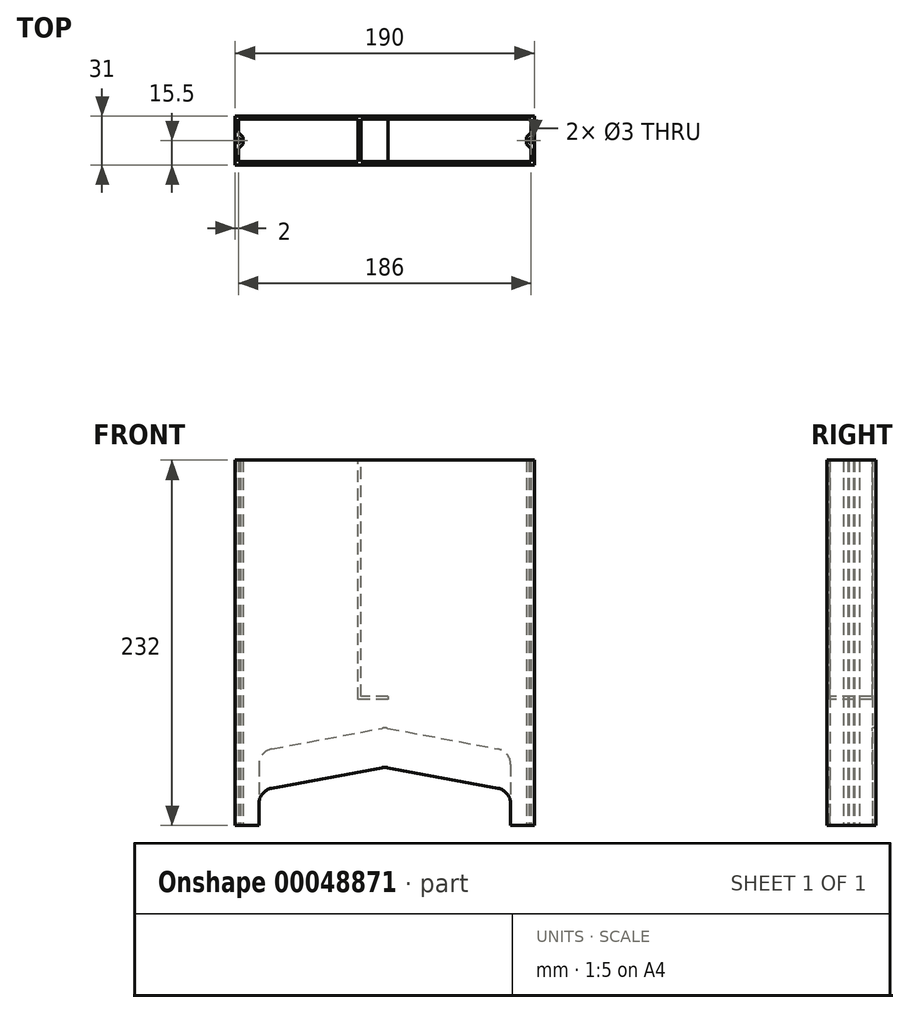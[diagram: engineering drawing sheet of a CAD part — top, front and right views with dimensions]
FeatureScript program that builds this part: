
annotation { "Feature Type Name" : "Feature", "Feature Type Description" : "" }
export const myFeature = defineFeature(function(context is Context, id is Id, definition is map)
    precondition{}
    {
        {
            var Q0;
            Q0=qCreatedBy(makeId("Top.planeOp"),FACE);
            var sketch = newSketch(context, id + "F0", { "sketchPlane" : qUnion([Q0])});
            skLineSegment(sketch, "E0.bottom", {"start": v(0, 0) * mm, "end": v(190, 0) * mm});
            skLineSegment(sketch, "E0.top", {"start": v(0, 31) * mm, "end": v(190, 31) * mm});
            skLineSegment(sketch, "E0.left", {"start": v(0, 0) * mm, "end": v(0, 31) * mm});
            skLineSegment(sketch, "E0.right", {"start": v(190, 0) * mm, "end": v(190, 31) * mm});
            skLineSegment(sketch, "E1.bottom", {"start": v(2, 2) * mm, "end": v(188, 2) * mm});
            skLineSegment(sketch, "E1.top", {"start": v(2, 29) * mm, "end": v(188, 29) * mm});
            skLineSegment(sketch, "E2", {"start": v(2, 29) * mm, "end": v(2, 20.62) * mm});
            skLineSegment(sketch, "E3", {"start": v(2, 20.62) * mm, "end": v(5, 17.62) * mm});
            skLineSegment(sketch, "E4", {"start": v(5, 17.62) * mm, "end": v(5, 13.38) * mm});
            skLineSegment(sketch, "E5", {"start": v(5, 13.38) * mm, "end": v(2, 10.38) * mm});
            skLineSegment(sketch, "E6", {"start": v(2, 10.38) * mm, "end": v(2, 2) * mm});
            skLineSegment(sketch, "E7", {"start": v(2, 20.62) * mm, "end": v(2, 10.38) * mm, "construction": true});
            skCircle(sketch, "E8", {"center": v(2, 15.5) * mm, "radius": 1.5 * mm});
            skLineSegment(sketch, "E9", {"start": v(95, 29) * mm, "end": v(95, 2) * mm, "construction": true});
            skLineSegment(sketch, "E10.MirrorCS", {"start": v(188, 10.38) * mm, "end": v(188, 2) * mm});
            skLineSegment(sketch, "E11.MirrorCS", {"start": v(185, 13.38) * mm, "end": v(188, 10.38) * mm});
            skLineSegment(sketch, "E12.MirrorCS", {"start": v(185, 17.62) * mm, "end": v(185, 13.38) * mm});
            skCircle(sketch, "E13.MirrorC", {"center": v(188, 15.5) * mm, "radius": 1.5 * mm});
            skLineSegment(sketch, "E14.MirrorCS", {"start": v(188, 29) * mm, "end": v(188, 20.62) * mm});
            skLineSegment(sketch, "E15.MirrorCS", {"start": v(188, 20.62) * mm, "end": v(185, 17.62) * mm});
            skSolve(sketch);
        }
        {
            var Q0;
            Q0=makeQuery(id+"F0.imprint","IMPRINT",FACE,{"disambiguationData":[TD([[makeQuery(id+"F0.imprint","IMPRINT",EDGE,{"derivedFrom":sQuery(id+"F0.wireOp",EDGE,"E0.bottom")}),1.0]])]});
            extrude(context, id + "F1", {"entities" : qUnion([Q0]), "depth" : 232 * mm});
        }
        {
            var Q0;
            Q0=makeQuery(id+"F1.opExtrude","SWEPT_FACE",FACE,{"disambiguationData":[OSD([sQuery(id+"F0.wireOp",EDGE,"E0.bottom")])]});
            var sketch = newSketch(context, id + "F2", { "sketchPlane" : qUnion([Q0])});
            skLineSegment(sketch, "E16.bottom", {"start": v(78, 232) * mm, "end": v(80, 232) * mm});
            skLineSegment(sketch, "E16.top", {"start": v(78, 80) * mm, "end": v(80, 80) * mm});
            skLineSegment(sketch, "E16.left", {"start": v(78, 232) * mm, "end": v(78, 80) * mm});
            skLineSegment(sketch, "E16.right", {"start": v(80, 232) * mm, "end": v(80, 80) * mm});
            skLineSegment(sketch, "E17.bottom", {"start": v(78, 80) * mm, "end": v(97, 80) * mm});
            skLineSegment(sketch, "E17.top", {"start": v(78, 82) * mm, "end": v(97, 82) * mm});
            skLineSegment(sketch, "E17.left", {"start": v(78, 80) * mm, "end": v(78, 82) * mm});
            skLineSegment(sketch, "E17.right", {"start": v(97, 80) * mm, "end": v(97, 82) * mm});
            skSolve(sketch);
        }
        {
            var Q0;
            Q0=qSketchRegion(id+"F2",true);
            extrude(context, id + "F3", {"entities" : qUnion([Q0]), "operationType" : NewBodyOperationType.ADD, "oppositeDirection" : true, "depth" : 29.5 * mm});
        }
        {
            var Q0;
            Q0=makeQuery(id+"F1.opExtrude","SWEPT_FACE",FACE,{"disambiguationData":[OSD([sQuery(id+"F0.wireOp",EDGE,"E0.top")])]});
            var sketch = newSketch(context, id + "F4", { "sketchPlane" : qUnion([Q0])});
            skLineSegment(sketch, "E18.bottom", {"start": v(-175, 47) * mm, "end": v(-15, 47) * mm});
            skLineSegment(sketch, "E18.top", {"start": v(-175, 0) * mm, "end": v(-15, 0) * mm});
            skLineSegment(sketch, "E18.left", {"start": v(-175, 47) * mm, "end": v(-175, 0) * mm});
            skLineSegment(sketch, "E18.right", {"start": v(-15, 47) * mm, "end": v(-15, 0) * mm});
            skLineSegment(sketch, "E19", {"start": v(-15, 47) * mm, "end": v(-95, 62) * mm});
            skLineSegment(sketch, "E20", {"start": v(-95, 62) * mm, "end": v(-175, 47) * mm});
            skSolve(sketch);
        }
        {
            var Q0;
            Q0 = qSketchRegion(id + "F4", true);
            extrude(context, id + "F5", {"entities" : qUnion([Q0]), "operationType" : NewBodyOperationType.REMOVE, "oppositeDirection" : true, "depth" : 5 * mm});
        }
        {
            var Q0;
            Q0=makeQuery(id+"F1.opExtrude","SWEPT_FACE",FACE,{"disambiguationData":[OSD([sQuery(id+"F0.wireOp",EDGE,"E0.bottom")])]});
            var sketch = newSketch(context, id + "F6", { "sketchPlane" : qUnion([Q0])});
            skLineSegment(sketch, "E21.bottom", {"start": v(15, 22) * mm, "end": v(175, 22) * mm});
            skLineSegment(sketch, "E21.top", {"start": v(15, 0) * mm, "end": v(175, 0) * mm});
            skLineSegment(sketch, "E21.left", {"start": v(15, 22) * mm, "end": v(15, 0) * mm});
            skLineSegment(sketch, "E21.right", {"start": v(175, 22) * mm, "end": v(175, 0) * mm});
            skLineSegment(sketch, "E22", {"start": v(15, 22) * mm, "end": v(95, 37) * mm});
            skLineSegment(sketch, "E23", {"start": v(95, 37) * mm, "end": v(175, 22) * mm});
            skSolve(sketch);
        }
        {
            var Q0;
            Q0 = qSketchRegion(id + "F6", true);
            extrude(context, id + "F7", {"entities" : qUnion([Q0]), "operationType" : NewBodyOperationType.REMOVE, "oppositeDirection" : true, "depth" : 5 * mm});
        }
        {
            var Q0;
            Q0=makeQuery(id+"F5.boolean.opBoolean","COPY",EDGE,{"derivedFrom":makeQuery(id+"F5.opExtrude","SWEPT_EDGE",EDGE,{"disambiguationData":[OSD([sQuery(id+"F4.wireOp",EDGE,"E18.bottom"),sQuery(id+"F4.wireOp",EDGE,"E18.right"),sQuery(id+"F4.wireOp",EDGE,"a8a949ac-19ef-4d88-9539-7b90844364a0")])]})});
            var Q1;
            Q1=makeQuery(id+"F7.boolean.opBoolean","COPY",EDGE,{"derivedFrom":makeQuery(id+"F7.opExtrude","SWEPT_EDGE",EDGE,{"disambiguationData":[OSD([sQuery(id+"F6.wireOp",EDGE,"E21.bottom"),sQuery(id+"F6.wireOp",EDGE,"E21.left"),sQuery(id+"F6.wireOp",EDGE,"1196cb7b-4268-45b7-9e53-025b5b560195")])]})});
            var Q2;
            Q2=makeQuery(id+"F5.boolean.opBoolean","COPY",EDGE,{"derivedFrom":makeQuery(id+"F5.opExtrude","SWEPT_EDGE",EDGE,{"disambiguationData":[OSD([sQuery(id+"F4.wireOp",EDGE,"E18.bottom"),sQuery(id+"F4.wireOp",EDGE,"E18.left"),sQuery(id+"F4.wireOp",EDGE,"a8a949ac-19ef-4d88-9539-7b90844364a0")])]})});
            var Q3;
            Q3=makeQuery(id+"F7.boolean.opBoolean","COPY",EDGE,{"derivedFrom":makeQuery(id+"F7.opExtrude","SWEPT_EDGE",EDGE,{"disambiguationData":[OSD([sQuery(id+"F6.wireOp",EDGE,"E21.bottom"),sQuery(id+"F6.wireOp",EDGE,"E21.right"),sQuery(id+"F6.wireOp",EDGE,"1196cb7b-4268-45b7-9e53-025b5b560195")])]})});
            var Q4;
            Q4=makeQuery(id+"F5.boolean.opBoolean","COPY",EDGE,{"derivedFrom":makeQuery(id+"F5.opExtrude","SWEPT_EDGE",EDGE,{"disambiguationData":[OSD([sQuery(id+"F4.wireOp",EDGE,"E19"),sQuery(id+"F4.wireOp",EDGE,"E20")])]})});
            var Q5;
            Q5=makeQuery(id+"F7.boolean.opBoolean","COPY",EDGE,{"derivedFrom":makeQuery(id+"F7.opExtrude","SWEPT_EDGE",EDGE,{"disambiguationData":[OSD([sQuery(id+"F6.wireOp",EDGE,"E22"),sQuery(id+"F6.wireOp",EDGE,"E23")])]})});
            fillet(context, id + "F8", {"entities" : qUnion([Q0, Q1, Q2, Q3, Q4, Q5]), "radius" : 10 * mm, "tangentPropagation" : true, "allowEdgeOverflow" : false});
        }
    });
